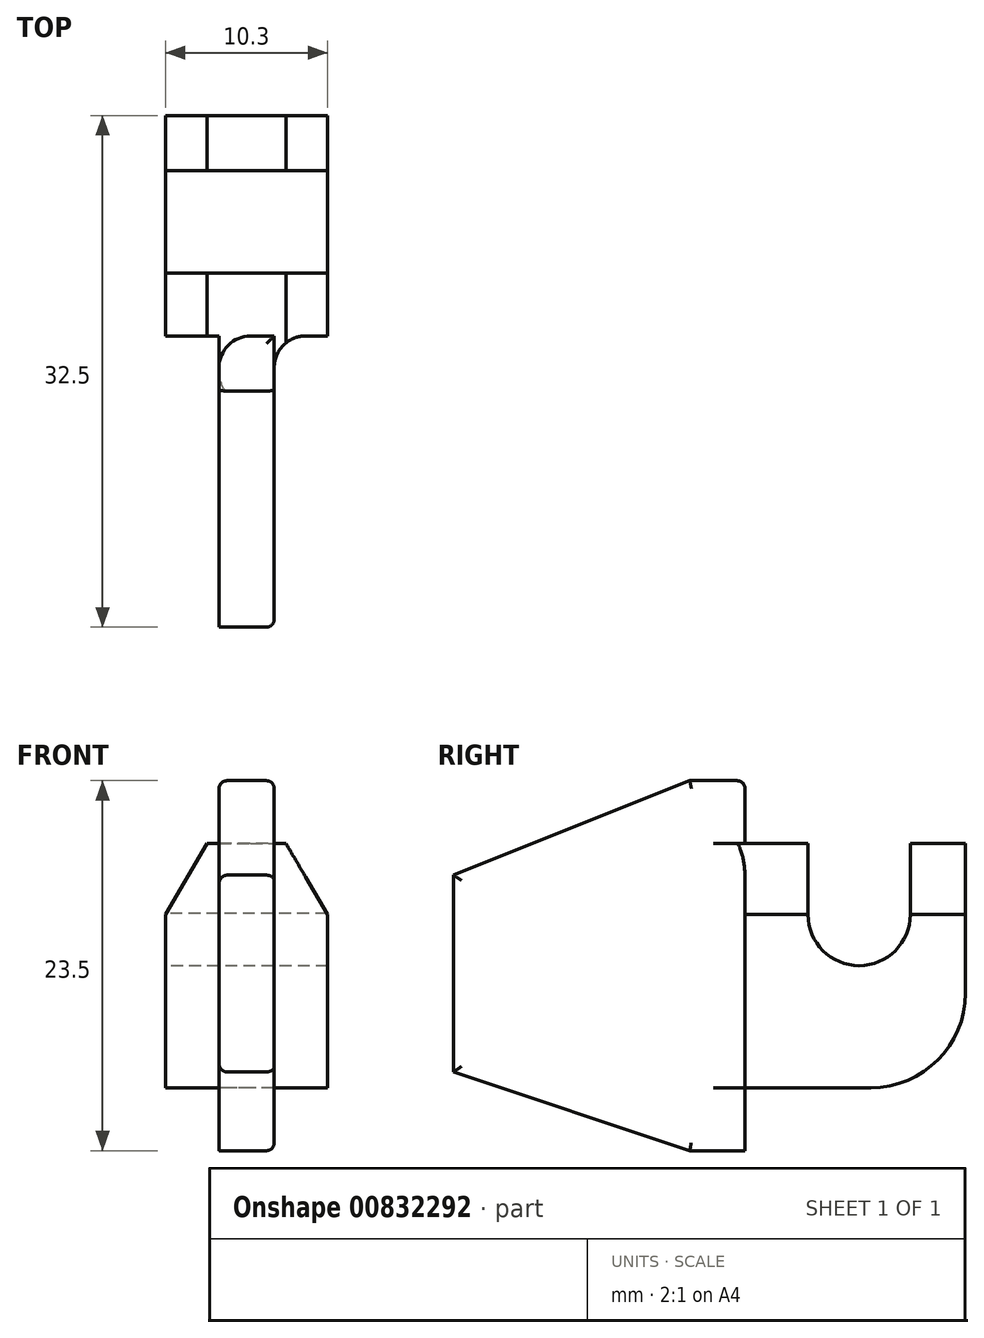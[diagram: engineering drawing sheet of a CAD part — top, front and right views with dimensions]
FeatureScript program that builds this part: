
annotation { "Feature Type Name" : "Feature", "Feature Type Description" : "" }
export const myFeature = defineFeature(function(context is Context, id is Id, definition is map)
    precondition{}
    {
        {
            var Q0;
            Q0=qCreatedBy(makeId("Front.planeOp"),FACE);
            var sketch = newSketch(context, id + "F0", { "sketchPlane" : qUnion([Q0])});
            skLineSegment(sketch, "E0.bottom", {"start": v(5.15, 5.5) * mm, "end": v(-5.15, 5.5) * mm});
            skLineSegment(sketch, "E0.top", {"start": v(5.15, -5.5) * mm, "end": v(-5.15, -5.5) * mm});
            skLineSegment(sketch, "E0.left", {"start": v(5.15, 5.5) * mm, "end": v(5.15, -5.5) * mm});
            skLineSegment(sketch, "E0.right", {"start": v(-5.15, 5.5) * mm, "end": v(-5.15, -5.5) * mm});
            skPoint(sketch, "E0.middle", {"position": v(0, 0) * mm});
            skLineSegment(sketch, "E1", {"start": v(-2.5, 10) * mm, "end": v(2.5, 10) * mm});
            skLineSegment(sketch, "E2", {"start": v(-2.5, 10) * mm, "end": v(-5.15, 5.5) * mm});
            skLineSegment(sketch, "E3", {"start": v(2.5, 10) * mm, "end": v(5.15, 5.5) * mm});
            skLineSegment(sketch, "E4", {"start": v(0, 13.52) * mm, "end": v(0, -10.49) * mm});
            skSolve(sketch);
        }
        {
            var Q0;
            Q0 = qSketchRegion(id + "F0", true);
            extrude(context, id + "F1", {"entities" : qUnion([Q0]), "oppositeDirection" : true, "depth" : 14 * mm, "offsetDistance" : 25 * mm});
        }
        {
            var Q0;
            Q0=qCreatedBy(makeId("Right.planeOp"),FACE);
            var sketch = newSketch(context, id + "F2", { "sketchPlane" : qUnion([Q0])});
            skArc(sketch, "E5", {"start": v(4, 5.5) * mm, "mid": v(7.28, 2.25) * mm, "end": v(10.5, 5.57) * mm});
            skLineSegment(sketch, "E6", {"start": v(4, 5.5) * mm, "end": v(4, 10) * mm});
            skLineSegment(sketch, "E7", {"start": v(4, 10) * mm, "end": v(10.5, 10) * mm});
            skLineSegment(sketch, "E8", {"start": v(10.5, 10) * mm, "end": v(10.5, 5.57) * mm});
            skSolve(sketch);
        }
        {
            var Q0;
            Q0 = qSketchRegion(id + "F2", true);
            extrude(context, id + "F3", {"entities" : qUnion([Q0]), "operationType" : NewBodyOperationType.REMOVE, "endBound" : BoundingType.THROUGH_ALL, "depth" : 25 * mm, "hasOffset" : true, "offsetDistance" : 50 * mm, "hasSecondDirection" : true, "secondDirectionBound" : SecondDirectionBoundingType.THROUGH_ALL, "secondDirectionOppositeDirection" : true, "secondDirectionDepth" : 50 * mm});
        }
        {
            var Q0;
            Q0=qCreatedBy(makeId("Right.planeOp"),FACE);
            var sketch = newSketch(context, id + "F4", { "sketchPlane" : qUnion([Q0])});
            skLineSegment(sketch, "E9", {"start": v(0, 0) * mm, "end": v(0, 14) * mm});
            skLineSegment(sketch, "E10", {"start": v(0, 14) * mm, "end": v(-3.5, 14) * mm});
            skLineSegment(sketch, "E11", {"start": v(0, 0) * mm, "end": v(0, -9.5) * mm});
            skLineSegment(sketch, "E12", {"start": v(0, -9.5) * mm, "end": v(-3.5, -9.5) * mm});
            skLineSegment(sketch, "E13", {"start": v(-18.5, -4.5) * mm, "end": v(-18.5, 8) * mm});
            skLineSegment(sketch, "E14", {"start": v(-18.5, -4.5) * mm, "end": v(-3.5, -9.5) * mm});
            skLineSegment(sketch, "E15", {"start": v(-18.5, 8) * mm, "end": v(-3.5, 14) * mm});
            skSolve(sketch);
        }
        {
            var Q0;
            Q0 = qSketchRegion(id + "F4", true);
            extrude(context, id + "F5", {"entities" : qUnion([Q0]), "operationType" : NewBodyOperationType.ADD, "endBound" : BoundingType.SYMMETRIC, "depth" : 3.5 * mm, "offsetDistance" : 25 * mm});
        }
        {
            var Q0;
            Q0=makeQuery(id+"F1.opExtrude","CAP_EDGE",EDGE,{"disambiguationData":[OSD([sQuery(id+"F0.wireOp",EDGE,"E0.top")])],"isStart":false});
            fillet(context, id + "F6", {"entities" : qUnion([Q0]), "radius" : 6 * mm, "tangentPropagation" : true, "allowEdgeOverflow" : false});
        }
        {
            var Q0;
            {var subQ0=sQuery(id+"F4.wireOp",EDGE,"E11");var subQ1=sQuery(id+"F4.wireOp",EDGE,"E9");Q0=makeQuery(id+"F5.boolean.opBoolean","SPLIT",EDGE,{"disambiguationData":[topologyDisambiguationEdgeConnected([makeQuery(id+"F1.opExtrude","CAP_FACE",FACE,{"disambiguationData":[OSD([sQuery(id+"F0.wireOp",EDGE,"E0.top"),sQuery(id+"F0.wireOp",EDGE,"E0.left"),sQuery(id+"F0.wireOp",EDGE,"E0.right"),sQuery(id+"F0.wireOp",EDGE,"E1"),sQuery(id+"F0.wireOp",EDGE,"E2"),sQuery(id+"F0.wireOp",EDGE,"E3")])],"isStart":true}),makeQuery(id+"F5.opExtrude","CAP_FACE",FACE,{"disambiguationData":[OSD([subQ1,sQuery(id+"F4.wireOp",EDGE,"E10"),subQ0,sQuery(id+"F4.wireOp",EDGE,"E12"),sQuery(id+"F4.wireOp",EDGE,"E13"),sQuery(id+"F4.wireOp",EDGE,"E14"),sQuery(id+"F4.wireOp",EDGE,"E15")])],"isStart":false})])],"derivedFrom":makeQuery(id+"F5.opExtrude","CAP_EDGE",EDGE,{"disambiguationData":[OSD([subQ1,subQ0])],"isStart":false})});}
            var Q1;
            {var subQ0=sQuery(id+"F4.wireOp",EDGE,"E11");var subQ1=sQuery(id+"F4.wireOp",EDGE,"E9");Q1=makeQuery(id+"F5.boolean.opBoolean","SPLIT",EDGE,{"disambiguationData":[topologyDisambiguationEdgeConnected([makeQuery(id+"F1.opExtrude","CAP_FACE",FACE,{"disambiguationData":[OSD([sQuery(id+"F0.wireOp",EDGE,"E0.top"),sQuery(id+"F0.wireOp",EDGE,"E0.left"),sQuery(id+"F0.wireOp",EDGE,"E0.right"),sQuery(id+"F0.wireOp",EDGE,"E1"),sQuery(id+"F0.wireOp",EDGE,"E2"),sQuery(id+"F0.wireOp",EDGE,"E3")])],"isStart":true}),makeQuery(id+"F5.opExtrude","CAP_FACE",FACE,{"disambiguationData":[OSD([subQ1,sQuery(id+"F4.wireOp",EDGE,"E10"),subQ0,sQuery(id+"F4.wireOp",EDGE,"E12"),sQuery(id+"F4.wireOp",EDGE,"E13"),sQuery(id+"F4.wireOp",EDGE,"E14"),sQuery(id+"F4.wireOp",EDGE,"E15")])],"isStart":true})])],"derivedFrom":makeQuery(id+"F5.opExtrude","CAP_EDGE",EDGE,{"disambiguationData":[OSD([subQ1,subQ0])],"isStart":true})});}
            fillet(context, id + "F7", {"entities" : qUnion([Q0, Q1]), "radius" : 2 * mm, "tangentPropagation" : true, "allowEdgeOverflow" : false});
        }
        {
            var Q0;
            Q0=makeQuery(id+"F5.opExtrude","CAP_EDGE",EDGE,{"disambiguationData":[OSD([sQuery(id+"F4.wireOp",EDGE,"E15")])],"isStart":false});
            var Q1;
            Q1=makeQuery(id+"F5.opExtrude","CAP_EDGE",EDGE,{"disambiguationData":[OSD([sQuery(id+"F4.wireOp",EDGE,"E10")])],"isStart":false});
            var Q2;
            Q2=makeQuery(id+"F5.opExtrude","CAP_EDGE",EDGE,{"disambiguationData":[OSD([sQuery(id+"F4.wireOp",EDGE,"E13")])],"isStart":false});
            var Q3;
            Q3=makeQuery(id+"F5.opExtrude","CAP_EDGE",EDGE,{"disambiguationData":[OSD([sQuery(id+"F4.wireOp",EDGE,"E14")])],"isStart":false});
            var Q4;
            Q4=makeQuery(id+"F5.opExtrude","CAP_EDGE",EDGE,{"disambiguationData":[OSD([sQuery(id+"F4.wireOp",EDGE,"E12")])],"isStart":false});
            var Q5;
            Q5=makeQuery(id+"F5.opExtrude","CAP_EDGE",EDGE,{"disambiguationData":[OSD([sQuery(id+"F4.wireOp",EDGE,"E15")])],"isStart":true});
            var Q6;
            Q6=makeQuery(id+"F5.opExtrude","CAP_EDGE",EDGE,{"disambiguationData":[OSD([sQuery(id+"F4.wireOp",EDGE,"E10")])],"isStart":true});
            var Q7;
            Q7=makeQuery(id+"F5.opExtrude","CAP_EDGE",EDGE,{"disambiguationData":[OSD([sQuery(id+"F4.wireOp",EDGE,"E14")])],"isStart":true});
            fillet(context, id + "F8", {"entities" : qUnion([Q0, Q1, Q2, Q3, Q4, Q5, Q6, Q7]), "radius" : .5 * mm, "tangentPropagation" : true, "allowEdgeOverflow" : false});
        }
    });
